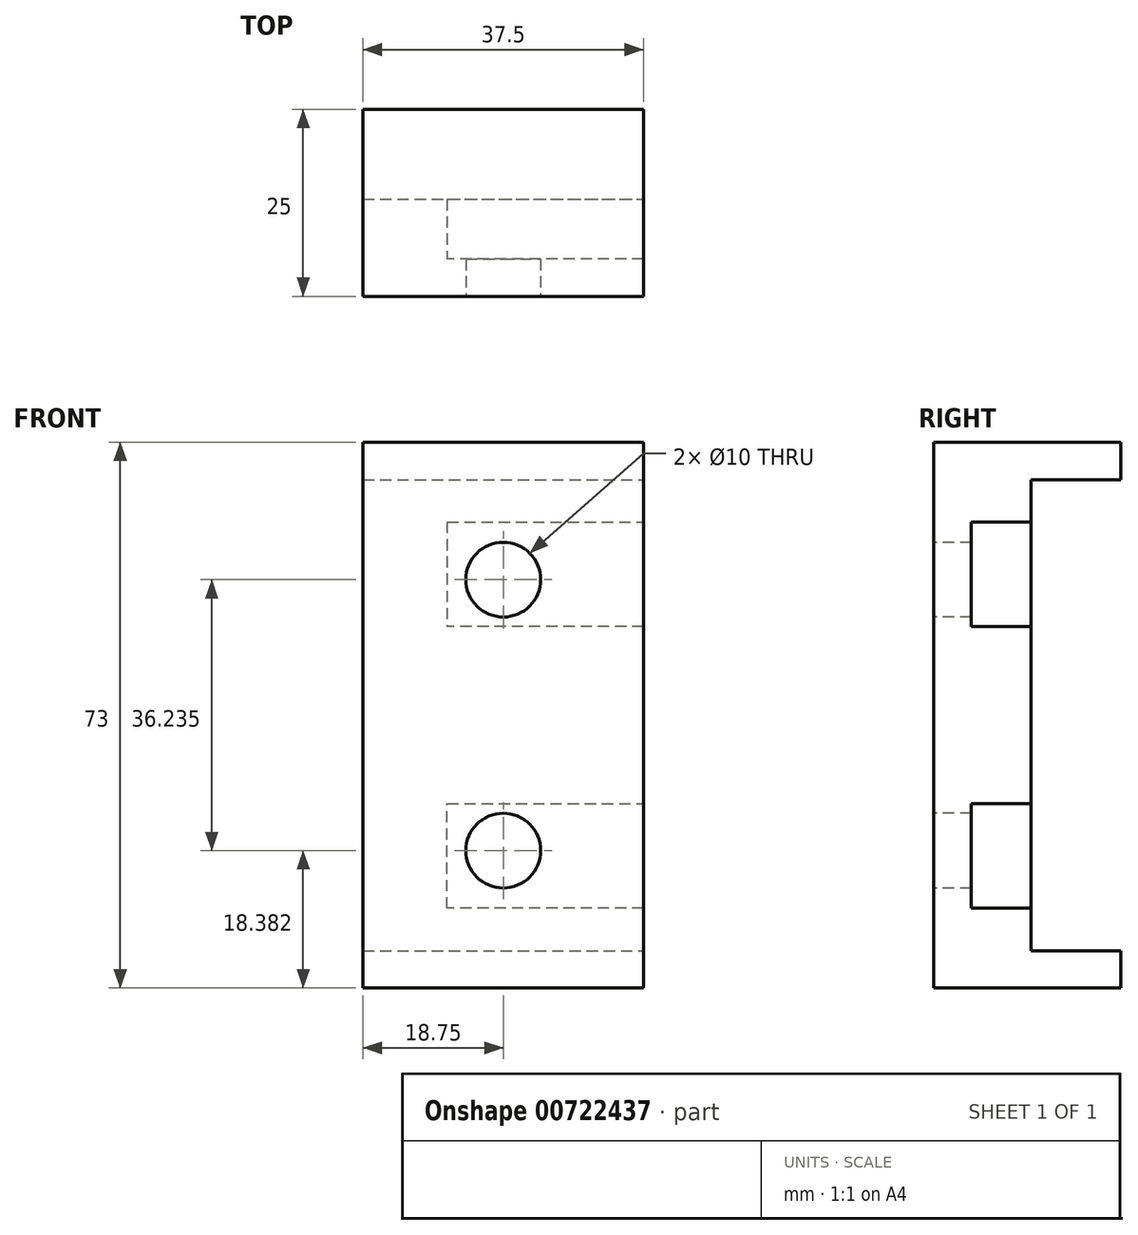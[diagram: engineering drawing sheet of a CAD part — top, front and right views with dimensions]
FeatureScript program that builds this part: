
annotation { "Feature Type Name" : "Feature", "Feature Type Description" : "" }
export const myFeature = defineFeature(function(context is Context, id is Id, definition is map)
    precondition{}
    {
        {
            var Q0;
            Q0=qCreatedBy(makeId("Front.planeOp"),FACE);
            var sketch = newSketch(context, id + "F0", { "sketchPlane" : qUnion([Q0])});
            skLineSegment(sketch, "E0.bottom", {"start": v(-18.75, 31.5) * mm, "end": v(18.75, 31.5) * mm});
            skLineSegment(sketch, "E0.top", {"start": v(-18.75, -31.5) * mm, "end": v(18.75, -31.5) * mm});
            skLineSegment(sketch, "E0.left", {"start": v(-18.75, 31.5) * mm, "end": v(-18.75, -31.5) * mm});
            skLineSegment(sketch, "E0.right", {"start": v(18.75, 31.5) * mm, "end": v(18.75, -31.5) * mm});
            skPoint(sketch, "E0.middle", {"position": v(0, 0) * mm});
            skSolve(sketch);
        }
        {
            var Q0;
            Q0=makeQuery(id+"F0.imprint","IMPRINT",FACE,{"disambiguationData":[TD([[makeQuery(id+"F0.imprint","IMPRINT",EDGE,{"derivedFrom":sQuery(id+"F0.wireOp",EDGE,"E0.bottom")}),-1.0]])]});
            var sketch = newSketch(context, id + "F1", { "sketchPlane" : qUnion([Q0])});
            skCircle(sketch, "E1", {"center": v(0, 18.12) * mm, "radius": 5 * mm});
            skCircle(sketch, "E2.MirrorC", {"center": v(0, -18.12) * mm, "radius": 5 * mm});
            skSolve(sketch);
        }
        {
            var Q0;
            Q0=makeQuery(id+"F0.imprint","IMPRINT",FACE,{"disambiguationData":[TD([[makeQuery(id+"F0.imprint","IMPRINT",EDGE,{"derivedFrom":sQuery(id+"F0.wireOp",EDGE,"E0.bottom")}),-1.0]])]});
            var sketch = newSketch(context, id + "F2", { "sketchPlane" : qUnion([Q0])});
            skSolve(sketch);
        }
        {
            var Q0;
            Q0 = qSketchRegion(id + "F0", true);
            extrude(context, id + "F3", {"entities" : qUnion([Q0]), "depth" : -5 * mm, "offsetDistance" : 25 * mm});
        }
        {
            var Q0;
            Q0=makeQuery(id+"F3.opExtrude","CAP_FACE",FACE,{"disambiguationData":[OSD([sQuery(id+"F0.wireOp",EDGE,"E0.bottom"),sQuery(id+"F0.wireOp",EDGE,"E0.top"),sQuery(id+"F0.wireOp",EDGE,"E0.left"),sQuery(id+"F0.wireOp",EDGE,"E0.right")])],"isStart":false});
            var sketch = newSketch(context, id + "F4", { "sketchPlane" : qUnion([Q0])});
            skLineSegment(sketch, "E3.bottom", {"start": v(0, 18.84) * mm, "end": v(-18.75, 18.84) * mm});
            skLineSegment(sketch, "E3.top", {"start": v(0, 11.84) * mm, "end": v(-18.75, 11.84) * mm});
            skLineSegment(sketch, "E3.left", {"start": v(0, 18.84) * mm, "end": v(0, 11.84) * mm});
            skLineSegment(sketch, "E3.right", {"start": v(-18.75, 18.84) * mm, "end": v(-18.75, 11.84) * mm});
            skLineSegment(sketch, "E4.top", {"start": v(0, 25.84) * mm, "end": v(-18.75, 25.84) * mm});
            skLineSegment(sketch, "E4.left", {"start": v(0, 18.84) * mm, "end": v(0, 25.84) * mm});
            skLineSegment(sketch, "E4.right", {"start": v(-18.75, 18.84) * mm, "end": v(-18.75, 25.84) * mm});
            skLineSegment(sketch, "E5.bottom", {"start": v(0, 25.84) * mm, "end": v(7.5, 25.84) * mm});
            skLineSegment(sketch, "E5.top", {"start": v(0, 11.84) * mm, "end": v(7.5, 11.84) * mm});
            skLineSegment(sketch, "E5.left", {"start": v(0, 25.84) * mm, "end": v(0, 11.84) * mm});
            skLineSegment(sketch, "E5.right", {"start": v(7.5, 25.84) * mm, "end": v(7.5, 11.84) * mm});
            skLineSegment(sketch, "E6.MirrorCS", {"start": v(0, -11.84) * mm, "end": v(-18.75, -11.84) * mm});
            skLineSegment(sketch, "E7.MirrorCS", {"start": v(0, -11.84) * mm, "end": v(7.5, -11.84) * mm});
            skLineSegment(sketch, "E8.MirrorCS", {"start": v(0, -18.84) * mm, "end": v(0, -11.84) * mm});
            skLineSegment(sketch, "E9.MirrorCS", {"start": v(0, -18.84) * mm, "end": v(0, -25.84) * mm});
            skLineSegment(sketch, "E10.MirrorCS", {"start": v(0, -18.84) * mm, "end": v(-18.75, -18.84) * mm});
            skLineSegment(sketch, "E11.MirrorCS", {"start": v(0, -25.84) * mm, "end": v(7.5, -25.84) * mm});
            skLineSegment(sketch, "E12.MirrorCS", {"start": v(7.5, -25.84) * mm, "end": v(7.5, -11.84) * mm});
            skLineSegment(sketch, "E13", {"start": v(0, -25.84) * mm, "end": v(-18.75, -25.84) * mm});
            skSolve(sketch);
        }
        {
            var Q0;
            {var subQ0=sQuery(id+"F4.wireOp",EDGE,"E3.top");Q0=makeQuery(id+"F4.imprint","IMPRINT",FACE,{"disambiguationData":[TD([[makeQuery(id+"F4.imprint","IMPRINT",EDGE,{"derivedFrom":subQ0}),1.0]])]});}
            extrude(context, id + "F5", {"entities" : qUnion([Q0]), "operationType" : NewBodyOperationType.ADD, "depth" : 8 * mm, "offsetDistance" : 25 * mm});
        }
        {
            var Q0;
            Q0=qCreatedBy(makeId("Front.planeOp"),FACE);
            var sketch = newSketch(context, id + "F6", { "sketchPlane" : qUnion([Q0])});
            skLineSegment(sketch, "E14.bottom", {"start": v(-18.75, 31.5) * mm, "end": v(18.75, 31.5) * mm});
            skLineSegment(sketch, "E14.top", {"start": v(-18.75, 36.5) * mm, "end": v(18.75, 36.5) * mm});
            skLineSegment(sketch, "E14.left", {"start": v(-18.75, 31.5) * mm, "end": v(-18.75, 36.5) * mm});
            skLineSegment(sketch, "E14.right", {"start": v(18.75, 31.5) * mm, "end": v(18.75, 36.5) * mm});
            skSolve(sketch);
        }
        {
            var Q0;
            Q0=makeQuery(id+"F6.imprint","IMPRINT",FACE,{"disambiguationData":[TD([[makeQuery(id+"F6.imprint","IMPRINT",EDGE,{"derivedFrom":sQuery(id+"F6.wireOp",EDGE,"E14.bottom")}),1.0]])]});
            extrude(context, id + "F7", {"entities" : qUnion([Q0]), "operationType" : NewBodyOperationType.ADD, "depth" : -25 * mm, "offsetDistance" : 25 * mm});
        }
        {
            var Q0;
            Q0=qCreatedBy(makeId("Front.planeOp"),FACE);
            var sketch = newSketch(context, id + "F8", { "sketchPlane" : qUnion([Q0])});
            skLineSegment(sketch, "E15.bottom", {"start": v(18.75, -31.5) * mm, "end": v(-18.75, -31.5) * mm});
            skLineSegment(sketch, "E15.top", {"start": v(18.75, -36.5) * mm, "end": v(-18.75, -36.5) * mm});
            skLineSegment(sketch, "E15.left", {"start": v(18.75, -31.5) * mm, "end": v(18.75, -36.5) * mm});
            skLineSegment(sketch, "E15.right", {"start": v(-18.75, -31.5) * mm, "end": v(-18.75, -36.5) * mm});
            skSolve(sketch);
        }
        {
            var Q0;
            Q0 = qSketchRegion(id + "F8", true);
            extrude(context, id + "F9", {"entities" : qUnion([Q0]), "operationType" : NewBodyOperationType.ADD, "depth" : -25 * mm, "offsetDistance" : 25 * mm});
        }
        {
            var Q0;
            Q0 = qSketchRegion(id + "F1", true);
            var Q1;
            Q1=sQuery(id+"F1.wireOp",EDGE,"E2.MirrorC");
            var Q2;
            Q2=sQuery(id+"F1.wireOp",EDGE,"E1");
            extrude(context, id + "F10", {"entities" : qUnion([Q0]), "operationType" : NewBodyOperationType.REMOVE, "surfaceEntities" : qUnion([Q1, Q2]), "oppositeDirection" : true, "depth" : 5 * mm, "offsetDistance" : 25 * mm});
        }
    });
